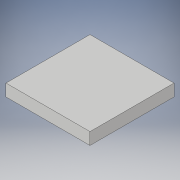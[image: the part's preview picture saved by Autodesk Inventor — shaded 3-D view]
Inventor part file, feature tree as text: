
AUTODESK INVENTOR PART (.ipt)
format: ipt  version: 2019 (Build 230136000, 136)  size: 213,504 bytes
history: native  units: mm
features: extrude x1, sketch x1
ambient origin geometry x8: Origin, YZ Plane, XZ Plane, XY Plane, X Axis, Y Axis, Z Axis, Center Point
bodies: Solid1 (feature_tree)
feature tree (2):
  extrude  "Extrusion1"  Depth=35.0mm
  sketch  "Sketch1"  dims[d0=35.0mm d1=35.0mm d2=5.0mm d3=0.0mm]
